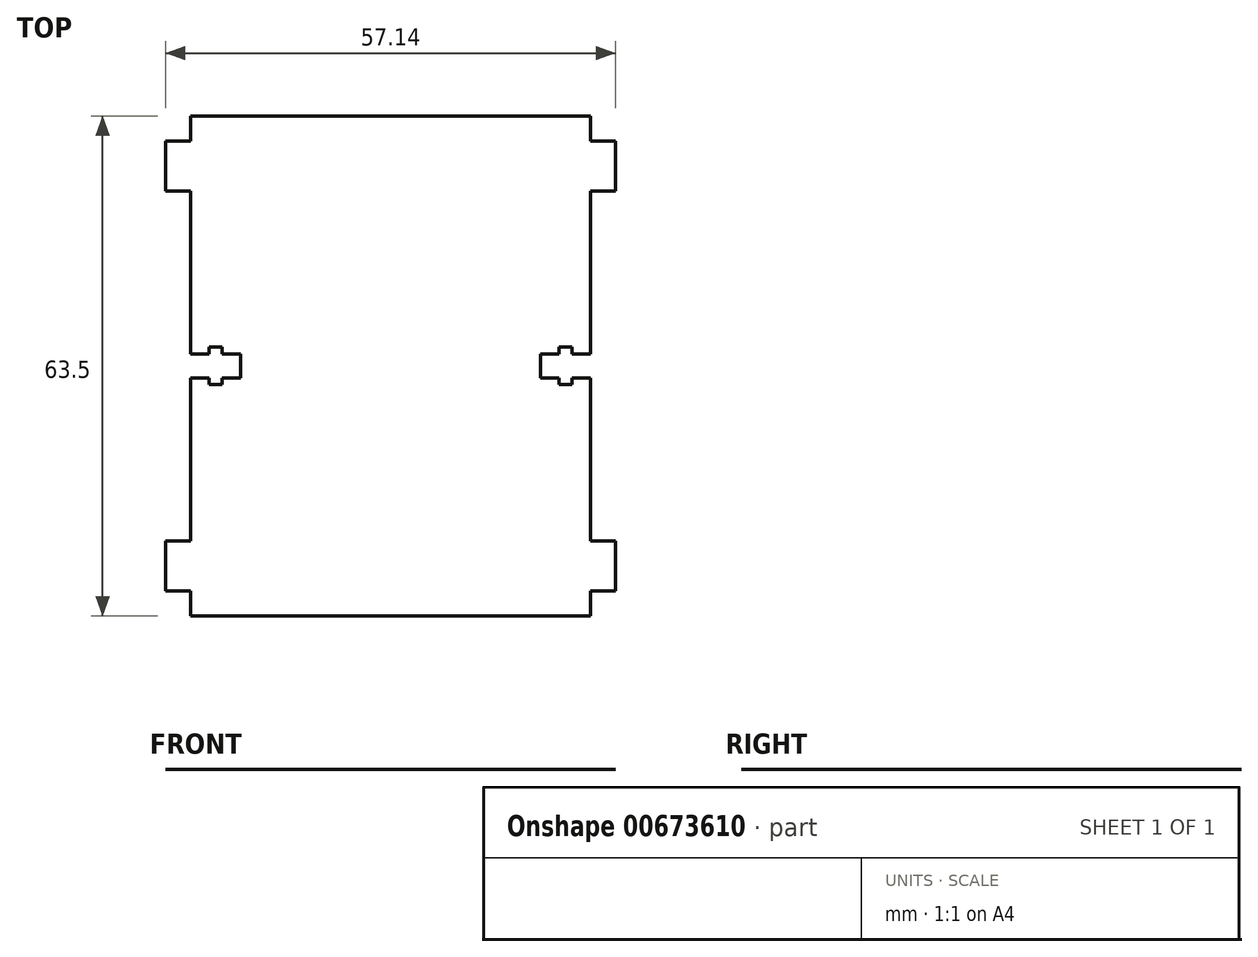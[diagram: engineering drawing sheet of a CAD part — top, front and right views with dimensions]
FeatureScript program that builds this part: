
annotation { "Feature Type Name" : "Feature", "Feature Type Description" : "" }
export const myFeature = defineFeature(function(context is Context, id is Id, definition is map)
    precondition{}
    {
        {
            var Q0;
            Q0=qCreatedBy(makeId("Top.planeOp"),FACE);
            var sketch = newSketch(context, id + "F0", { "sketchPlane" : qUnion([Q0])});
            skLineSegment(sketch, "E0.bottom", {"start": v(25.4, 31.75) * mm, "end": v(-25.4, 31.75) * mm});
            skLineSegment(sketch, "E0.top", {"start": v(25.4, -31.75) * mm, "end": v(-25.4, -31.75) * mm});
            skLineSegment(sketch, "E0.left", {"start": v(25.4, 31.75) * mm, "end": v(25.4, 28.58) * mm});
            skLineSegment(sketch, "E0.right", {"start": v(-25.4, 31.75) * mm, "end": v(-25.4, 28.58) * mm});
            skPoint(sketch, "E0.middle", {"position": v(0, 0) * mm});
            skLineSegment(sketch, "E1.bottom", {"start": v(28.57, 22.23) * mm, "end": v(25.4, 22.23) * mm});
            skLineSegment(sketch, "E1.top", {"start": v(28.58, 28.58) * mm, "end": v(25.4, 28.58) * mm});
            skLineSegment(sketch, "E1.left", {"start": v(28.58, 22.23) * mm, "end": v(28.58, 28.58) * mm});
            skPoint(sketch, "E1.middle", {"position": v(25.4, 25.4) * mm});
            skPoint(sketch, "E1.right.end.orphan", {"position": v(22.22, 28.58) * mm});
            skPoint(sketch, "E2.orphan", {"position": v(22.23, 22.23) * mm});
            skLineSegment(sketch, "E3.trimOffspring", {"start": v(25.4, 22.23) * mm, "end": v(25.4, 1.52) * mm});
            skLineSegment(sketch, "E4.MirrorCS", {"start": v(28.57, -22.23) * mm, "end": v(25.4, -22.23) * mm});
            skLineSegment(sketch, "E5.MirrorCS", {"start": v(28.58, -22.23) * mm, "end": v(28.58, -28.58) * mm});
            skLineSegment(sketch, "E6.MirrorCS", {"start": v(28.58, -28.58) * mm, "end": v(25.4, -28.58) * mm});
            skLineSegment(sketch, "E7.MirrorCS", {"start": v(-28.58, 28.58) * mm, "end": v(-25.4, 28.58) * mm});
            skLineSegment(sketch, "E8.MirrorCS", {"start": v(-28.58, 22.23) * mm, "end": v(-28.58, 28.58) * mm});
            skLineSegment(sketch, "E9.MirrorCS", {"start": v(-28.57, 22.23) * mm, "end": v(-25.4, 22.23) * mm});
            skLineSegment(sketch, "E10.MirrorCS", {"start": v(-28.57, -22.23) * mm, "end": v(-25.4, -22.23) * mm});
            skLineSegment(sketch, "E11.MirrorCS", {"start": v(-28.58, -22.23) * mm, "end": v(-28.58, -28.58) * mm});
            skLineSegment(sketch, "E12.MirrorCS", {"start": v(-28.58, -28.58) * mm, "end": v(-25.4, -28.58) * mm});
            skLineSegment(sketch, "E13.trimOffspring", {"start": v(-25.4, -28.58) * mm, "end": v(-25.4, -31.75) * mm});
            skLineSegment(sketch, "E14.trimOffspring", {"start": v(25.4, -28.58) * mm, "end": v(25.4, -31.75) * mm});
            skLineSegment(sketch, "E15.trimOffspring", {"start": v(-25.4, 22.23) * mm, "end": v(-25.4, 1.52) * mm});
            skLineSegment(sketch, "E16.bottom", {"start": v(25.4, 1.52) * mm, "end": v(23.06, 1.52) * mm});
            skLineSegment(sketch, "E16.top", {"start": v(25.4, -1.52) * mm, "end": v(23.06, -1.52) * mm});
            skLineSegment(sketch, "E16.right", {"start": v(19.05, 1.52) * mm, "end": v(19.05, -1.52) * mm});
            skPoint(sketch, "E16.middle", {"position": v(22.23, 0) * mm});
            skLineSegment(sketch, "E17.bottom", {"start": v(23.06, -2.38) * mm, "end": v(21.39, -2.38) * mm});
            skLineSegment(sketch, "E17.top", {"start": v(23.06, 2.38) * mm, "end": v(21.39, 2.38) * mm});
            skLineSegment(sketch, "E17.left", {"start": v(23.06, -2.38) * mm, "end": v(23.06, -1.52) * mm});
            skLineSegment(sketch, "E17.right", {"start": v(21.39, -2.38) * mm, "end": v(21.39, -1.52) * mm});
            skLineSegment(sketch, "E18.trimOffspring", {"start": v(21.39, 1.52) * mm, "end": v(19.05, 1.52) * mm});
            skLineSegment(sketch, "E19.trimOffspring", {"start": v(21.39, 1.52) * mm, "end": v(21.39, 2.38) * mm});
            skLineSegment(sketch, "E20.trimOffspring", {"start": v(21.39, -1.52) * mm, "end": v(19.05, -1.52) * mm});
            skLineSegment(sketch, "E21.trimOffspring", {"start": v(23.06, 1.52) * mm, "end": v(23.06, 2.38) * mm});
            skLineSegment(sketch, "E22.trimOffspring", {"start": v(25.4, -1.52) * mm, "end": v(25.4, -22.23) * mm});
            skLineSegment(sketch, "E23.MirrorCS", {"start": v(-25.4, -1.52) * mm, "end": v(-23.06, -1.52) * mm});
            skLineSegment(sketch, "E24.MirrorCS", {"start": v(-23.06, -2.38) * mm, "end": v(-23.06, -1.52) * mm});
            skLineSegment(sketch, "E25.MirrorCS", {"start": v(-23.06, -2.38) * mm, "end": v(-21.39, -2.38) * mm});
            skLineSegment(sketch, "E26.MirrorCS", {"start": v(-21.39, -2.38) * mm, "end": v(-21.39, -1.52) * mm});
            skLineSegment(sketch, "E27.MirrorCS", {"start": v(-21.39, -1.52) * mm, "end": v(-19.05, -1.52) * mm});
            skLineSegment(sketch, "E28.MirrorCS", {"start": v(-19.05, 1.52) * mm, "end": v(-19.05, -1.52) * mm});
            skLineSegment(sketch, "E29.MirrorCS", {"start": v(-21.39, 1.52) * mm, "end": v(-19.05, 1.52) * mm});
            skLineSegment(sketch, "E30.MirrorCS", {"start": v(-21.39, 1.52) * mm, "end": v(-21.39, 2.38) * mm});
            skLineSegment(sketch, "E31.MirrorCS", {"start": v(-23.06, 2.38) * mm, "end": v(-21.39, 2.38) * mm});
            skLineSegment(sketch, "E32.MirrorCS", {"start": v(-23.06, 1.52) * mm, "end": v(-23.06, 2.38) * mm});
            skLineSegment(sketch, "E33.MirrorCS", {"start": v(-25.4, 1.52) * mm, "end": v(-23.06, 1.52) * mm});
            skLineSegment(sketch, "E34.trimOffspring", {"start": v(-25.4, -1.52) * mm, "end": v(-25.4, -22.23) * mm});
            skSolve(sketch);
        }
        {
            var Q0;
            Q0=makeQuery(id+"F0.imprint","IMPRINT",FACE,{"disambiguationData":[TD([[makeQuery(id+"F0.imprint","IMPRINT",EDGE,{"derivedFrom":sQuery(id+"F0.wireOp",EDGE,"E0.bottom")}),1.0]])]});
            extrude(context, id + "F1", {"entities" : qUnion([Q0]), "depth" : 1 / 203.2 * mm});
        }
    });
